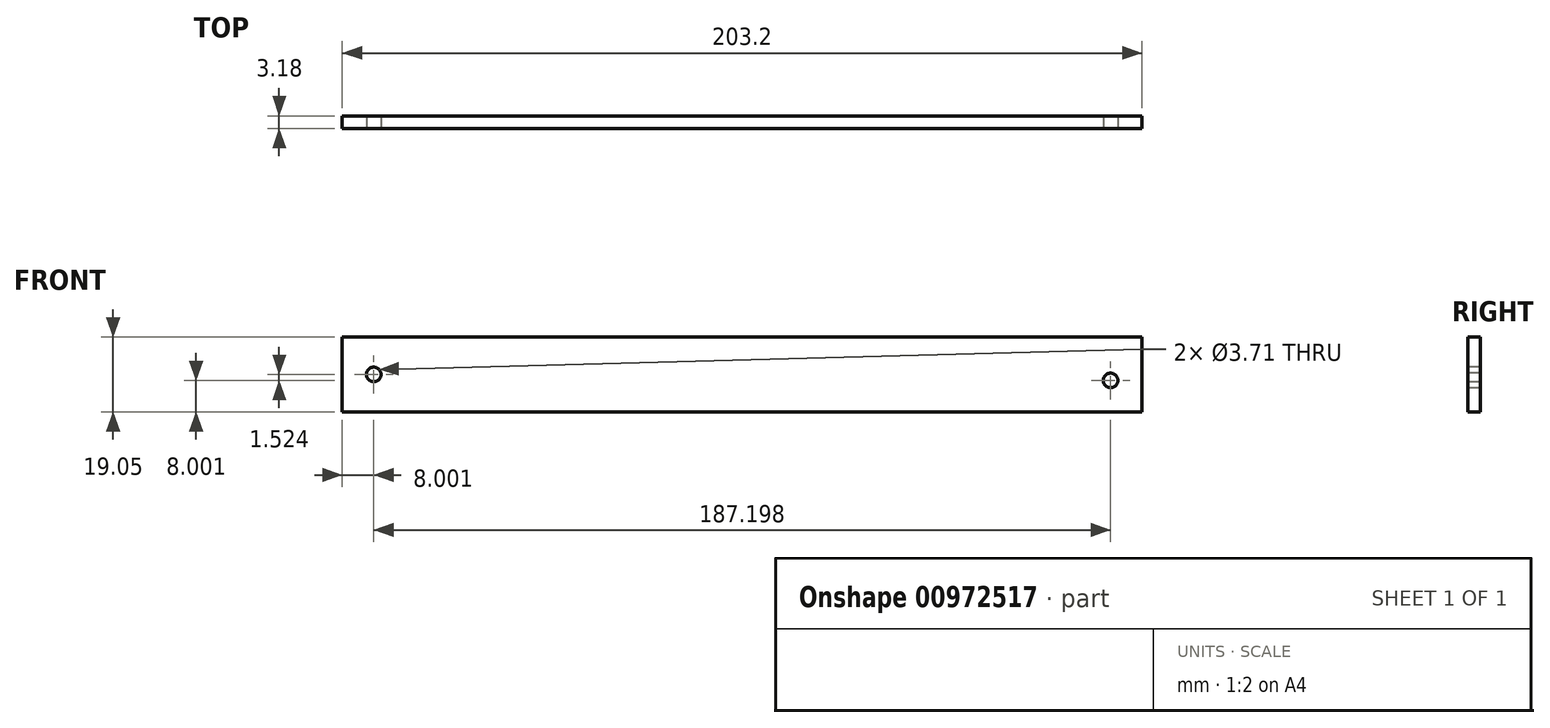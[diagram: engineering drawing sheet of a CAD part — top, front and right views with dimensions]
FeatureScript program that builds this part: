
annotation { "Feature Type Name" : "Feature", "Feature Type Description" : "" }
export const myFeature = defineFeature(function(context is Context, id is Id, definition is map)
    precondition{}
    {
        {
            var Q0;
            Q0=qCreatedBy(makeId("Front.planeOp"),FACE);
            var sketch = newSketch(context, id + "F0", { "sketchPlane" : qUnion([Q0])});
            skLineSegment(sketch, "E0.bottom", {"start": v(0, 0) * mm, "end": v(-203.2, 0) * mm});
            skLineSegment(sketch, "E0.top", {"start": v(0, 19.05) * mm, "end": v(-203.2, 19.05) * mm});
            skLineSegment(sketch, "E0.left", {"start": v(0, 0) * mm, "end": v(0, 19.05) * mm});
            skLineSegment(sketch, "E0.right", {"start": v(-203.2, 0) * mm, "end": v(-203.2, 19.05) * mm});
            skSolve(sketch);
        }
        {
            var Q0;
            Q0=makeQuery(id+"F0.imprint","IMPRINT",FACE,{"disambiguationData":[TD([[makeQuery(id+"F0.imprint","IMPRINT",EDGE,{"derivedFrom":sQuery(id+"F0.wireOp",EDGE,"E0.bottom")}),-1.0]])]});
            extrude(context, id + "F1", {"entities" : qUnion([Q0]), "depth" : 3.17 * mm, "offsetDistance" : 25.4 * mm});
        }
        {
            var Q0;
            Q0=makeQuery(id+"F1.opExtrude","CAP_FACE",FACE,{"disambiguationData":[OSD([sQuery(id+"F0.wireOp",EDGE,"E0.bottom"),sQuery(id+"F0.wireOp",EDGE,"E0.top"),sQuery(id+"F0.wireOp",EDGE,"E0.left"),sQuery(id+"F0.wireOp",EDGE,"E0.right")])],"isStart":false});
            var sketch = newSketch(context, id + "F2", { "sketchPlane" : qUnion([Q0])});
            skCircle(sketch, "E1", {"center": v(-195.2, 9.53) * mm, "radius": 1.85 * mm});
            skPoint(sketch, "E1.centerSnap0", {"position": v(-203.2, 9.53) * mm});
            skCircle(sketch, "E2", {"center": v(-8, 8) * mm, "radius": 1.85 * mm});
            skSolve(sketch);
        }
        {
            var Q0;
            Q0=makeQuery(id+"F2.imprint","IMPRINT",FACE,{"disambiguationData":[TD([[makeQuery(id+"F2.imprint","IMPRINT",EDGE,{"derivedFrom":sQuery(id+"F2.wireOp",EDGE,"E1")}),1.0]])]});
            var Q1;
            Q1=makeQuery(id+"F2.imprint","IMPRINT",FACE,{"disambiguationData":[TD([[makeQuery(id+"F2.imprint","IMPRINT",EDGE,{"derivedFrom":sQuery(id+"F2.wireOp",EDGE,"E2")}),1.0]])]});
            extrude(context, id + "F3", {"entities" : qUnion([Q0, Q1]), "operationType" : NewBodyOperationType.REMOVE, "oppositeDirection" : true, "depth" : 25.4 * mm, "offsetDistance" : 25.4 * mm});
        }
    });
